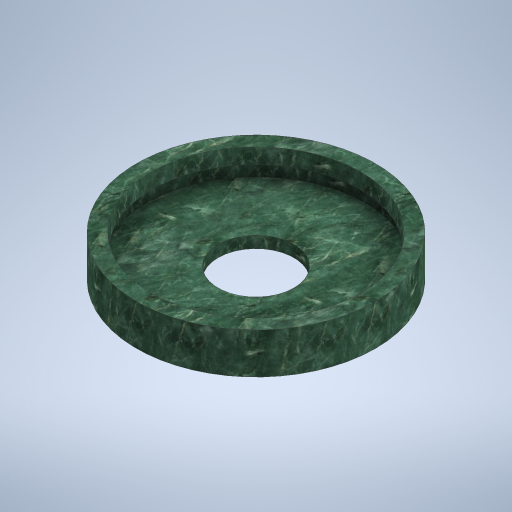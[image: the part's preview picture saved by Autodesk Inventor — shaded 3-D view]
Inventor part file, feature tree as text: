
AUTODESK INVENTOR PART (.ipt)
format: ipt  version: 2024 (Build 280153000, 153)  size: 392,192 bytes
history: native  units: in
note: dims shown in document units (in); Inventor stores cm internally (conversion verified against a paired STEP export)
features: revolve x1, direct_edit x1, sketch x1, other x1
ambient origin geometry x8: Origin, YZ Plane, XZ Plane, XY Plane, X Axis, Y Axis, Z Axis, Center Point
bodies: Solid1 (feature_tree)
feature tree (4):
  revolve  "Revolution1"  [1 undecoded]
  direct_edit  "Direct Edit1"
  sketch  "Sketch1"  dims[d0=0.13in d1=0.41in d2=0.07in d3=0.025in d4=0.356in d5=0.375in d6=0.02in d7=0.025in d8=90.0deg d9=3.937in d10=0.3937in d11=0.3937in]
  other  "Scale1"
note: 1 required parameter value undecoded (feature->parameter linkage not recoverable at this tier; creation-order binding heuristic only, values carry confidence <= 0.55)
